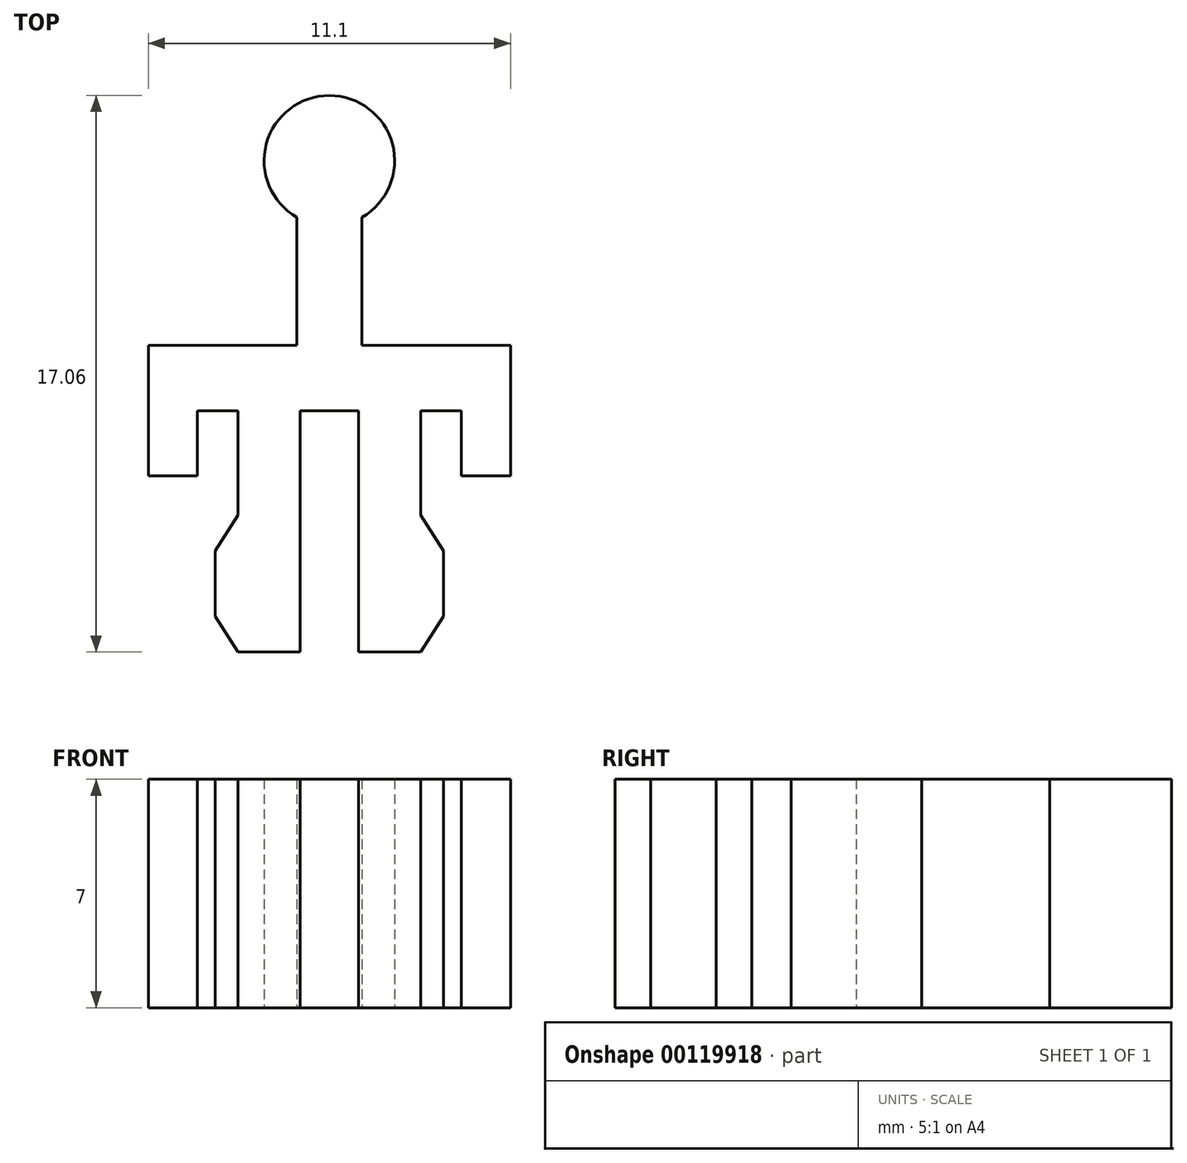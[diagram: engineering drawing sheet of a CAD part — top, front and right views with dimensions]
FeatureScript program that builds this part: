
annotation { "Feature Type Name" : "Feature", "Feature Type Description" : "" }
export const myFeature = defineFeature(function(context is Context, id is Id, definition is map)
    precondition{}
    {
        {
            var Q0;
            Q0=qCreatedBy(makeId("Top.planeOp"),FACE);
            var sketch = newSketch(context, id + "F0", { "sketchPlane" : qUnion([Q0])});
            skLineSegment(sketch, "E0.bottom", {"start": v(-0.9, 0) * mm, "end": v(-2.8, 0) * mm});
            skLineSegment(sketch, "E0.top", {"start": v(-0.9, -7.4) * mm, "end": v(-2.8, -7.4) * mm});
            skLineSegment(sketch, "E0.left", {"start": v(-0.9, 0) * mm, "end": v(-0.9, -7.4) * mm});
            skLineSegment(sketch, "E0.right", {"start": v(-2.8, 0) * mm, "end": v(-2.8, -7.4) * mm});
            skLineSegment(sketch, "E1", {"start": v(-2.8, -7.4) * mm, "end": v(-3.5, -6.3) * mm});
            skLineSegment(sketch, "E2", {"start": v(-3.5, -6.3) * mm, "end": v(-3.5, -4.3) * mm});
            skLineSegment(sketch, "E3", {"start": v(-3.5, -4.3) * mm, "end": v(-2.8, -3.2) * mm});
            skLineSegment(sketch, "E4", {"start": v(-2.8, 0) * mm, "end": v(-4.05, 0) * mm});
            skLineSegment(sketch, "E5", {"start": v(-4.05, 0) * mm, "end": v(-4.05, -2) * mm});
            skLineSegment(sketch, "E6", {"start": v(-4.05, -2) * mm, "end": v(-5.55, -2) * mm});
            skLineSegment(sketch, "E7", {"start": v(-5.55, -2) * mm, "end": v(-5.55, 2) * mm});
            skLineSegment(sketch, "E8", {"start": v(-5.55, 2) * mm, "end": v(0, 2) * mm});
            skLineSegment(sketch, "E9.MirrorCS", {"start": v(2.8, 0) * mm, "end": v(2.8, -7.4) * mm});
            skLineSegment(sketch, "E10.MirrorCS", {"start": v(0.9, 0) * mm, "end": v(0.9, -7.4) * mm});
            skLineSegment(sketch, "E11.MirrorCS", {"start": v(0.9, 0) * mm, "end": v(2.8, 0) * mm});
            skLineSegment(sketch, "E12.MirrorCS", {"start": v(5.55, -2) * mm, "end": v(5.55, 2) * mm});
            skLineSegment(sketch, "E13.MirrorCS", {"start": v(3.5, -4.3) * mm, "end": v(2.8, -3.2) * mm});
            skLineSegment(sketch, "E14.MirrorCS", {"start": v(0.9, -7.4) * mm, "end": v(2.8, -7.4) * mm});
            skLineSegment(sketch, "E15.MirrorCS", {"start": v(5.55, 2) * mm, "end": v(0, 2) * mm});
            skLineSegment(sketch, "E16.MirrorCS", {"start": v(2.8, -7.4) * mm, "end": v(3.5, -6.3) * mm});
            skLineSegment(sketch, "E17.MirrorCS", {"start": v(2.8, 0) * mm, "end": v(4.05, 0) * mm});
            skLineSegment(sketch, "E18.MirrorCS", {"start": v(3.5, -6.3) * mm, "end": v(3.5, -4.3) * mm});
            skLineSegment(sketch, "E19.MirrorCS", {"start": v(4.05, -2) * mm, "end": v(5.55, -2) * mm});
            skLineSegment(sketch, "E20.MirrorCS", {"start": v(4.05, 0) * mm, "end": v(4.05, -2) * mm});
            skLineSegment(sketch, "E21", {"start": v(-0.9, 0) * mm, "end": v(0.9, 0) * mm});
            skLineSegment(sketch, "E22.bottom", {"start": v(-1, 2) * mm, "end": v(1, 2) * mm});
            skLineSegment(sketch, "E22.top", {"start": v(-1, 7) * mm, "end": v(1, 7) * mm});
            skLineSegment(sketch, "E22.left", {"start": v(-1, 2) * mm, "end": v(-1, 7) * mm});
            skLineSegment(sketch, "E22.right", {"start": v(1, 2) * mm, "end": v(1, 7) * mm});
            skCircle(sketch, "E23", {"center": v(0, 7.66) * mm, "radius": 2 * mm});
            skPoint(sketch, "E23.centerSnap0", {"position": v(0, 7) * mm});
            skSolve(sketch);
        }
        {
            var Q0;
            Q0=qSketchRegion(id+"F0",true);
            extrude(context, id + "F1", {"entities" : qUnion([Q0]), "depth" : 7 * mm});
        }
    });
